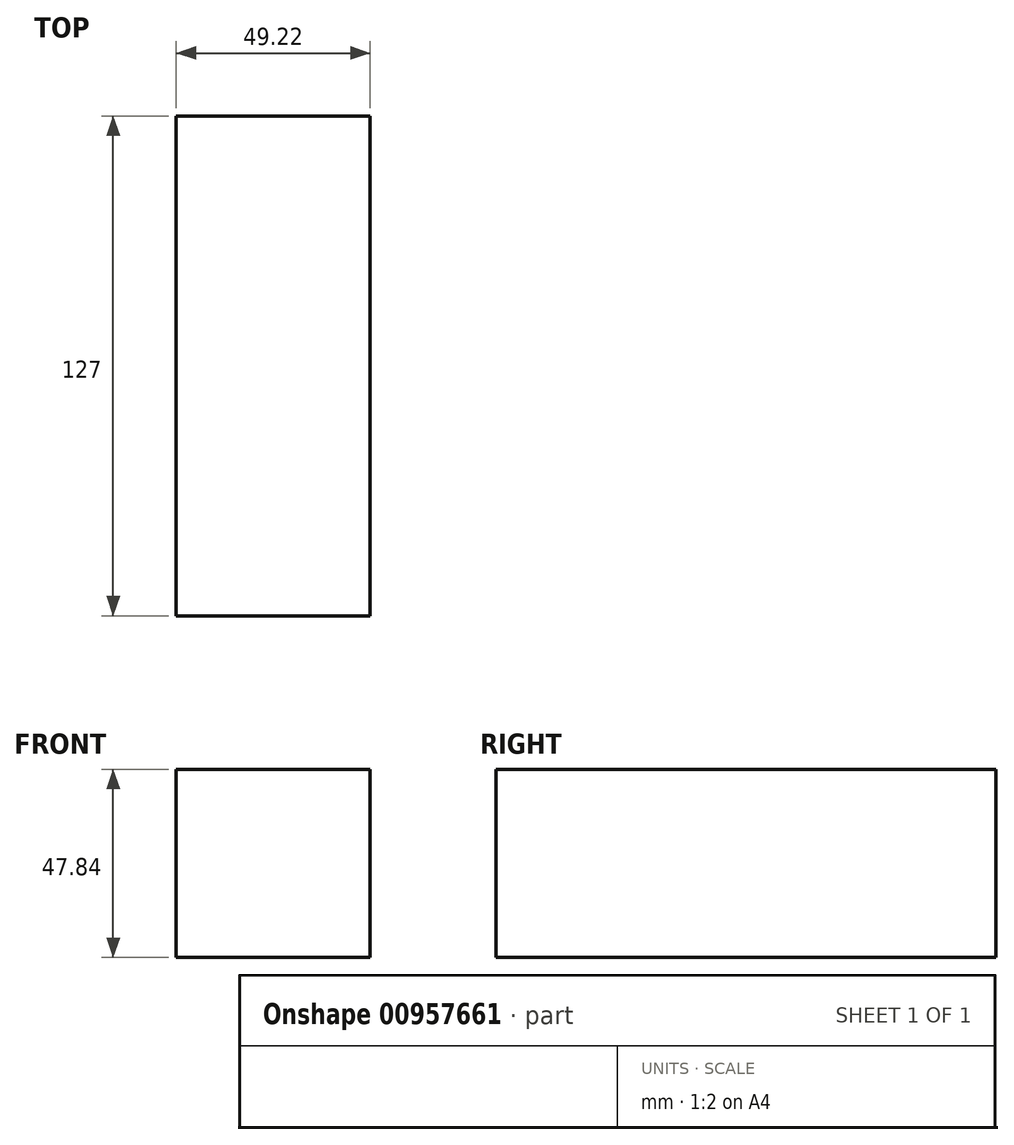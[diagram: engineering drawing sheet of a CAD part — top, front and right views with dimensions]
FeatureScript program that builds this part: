
annotation { "Feature Type Name" : "Feature", "Feature Type Description" : "" }
export const myFeature = defineFeature(function(context is Context, id is Id, definition is map)
    precondition{}
    {
        {
            var Q0;
            Q0=qCreatedBy(makeId("Front.planeOp"),FACE);
            var sketch = newSketch(context, id + "F0", { "sketchPlane" : qUnion([Q0])});
            skLineSegment(sketch, "E0.bottom", {"start": v(-40.46, 30.4) * mm, "end": v(8.75, 30.4) * mm});
            skLineSegment(sketch, "E0.top", {"start": v(-40.46, -17.44) * mm, "end": v(8.75, -17.44) * mm});
            skLineSegment(sketch, "E0.left", {"start": v(-40.46, 30.4) * mm, "end": v(-40.46, -17.44) * mm});
            skLineSegment(sketch, "E0.right", {"start": v(8.75, 30.4) * mm, "end": v(8.75, -17.44) * mm});
            skSolve(sketch);
        }
        {
            var Q0;
            Q0=makeQuery(id+"F0.imprint","IMPRINT",FACE,{"disambiguationData":[TD([[makeQuery(id+"F0.imprint","IMPRINT",EDGE,{"derivedFrom":sQuery(id+"F0.wireOp",EDGE,"E0.bottom")}),-1.0]])]});
            extrude(context, id + "F1", {"entities" : qUnion([Q0]), "depth" : 127 * mm, "offsetDistance" : 25.4 * mm});
        }
        {
            var Q0;
            Q0=makeQuery(id+"F1.opExtrude","SWEPT_BODY",BODY,{"disambiguationData":[OSD([sQuery(id+"F0.wireOp",EDGE,"E0.bottom"),sQuery(id+"F0.wireOp",EDGE,"E0.top"),sQuery(id+"F0.wireOp",EDGE,"E0.left"),sQuery(id+"F0.wireOp",EDGE,"E0.right")])]});
            transform(context, id + "F2", {"entities" : qUnion([Q0]), "transformType" : TransformType.TRANSLATION_3D, "dx" : -54.86 * mm, "dy" : -269.5 * mm, "dz" : 33.27 * mm, "makeCopy" : false});
        }
    });
